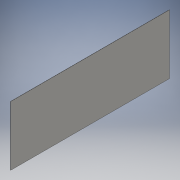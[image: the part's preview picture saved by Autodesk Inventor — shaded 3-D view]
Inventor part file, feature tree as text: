
AUTODESK INVENTOR PART (.ipt)
format: ipt  version: 2016 (Build 200138000, 138)  size: 84,480 bytes
history: native  units: in
note: dims shown in document units (in); Inventor stores cm internally (conversion verified against a paired STEP export)
features: extrude x1, sketch x1
ambient origin geometry x8: Origin, YZ Plane, XZ Plane, XY Plane, X Axis, Y Axis, Z Axis, Center Point
bodies: Solid1 (feature_tree)
feature tree (2):
  extrude  "Extrusion1"  Depth=12.0in
  sketch  "Sketch1"  dims[d0=4.5in d1=12.0in d2=0.0156in d3=0.0in]
